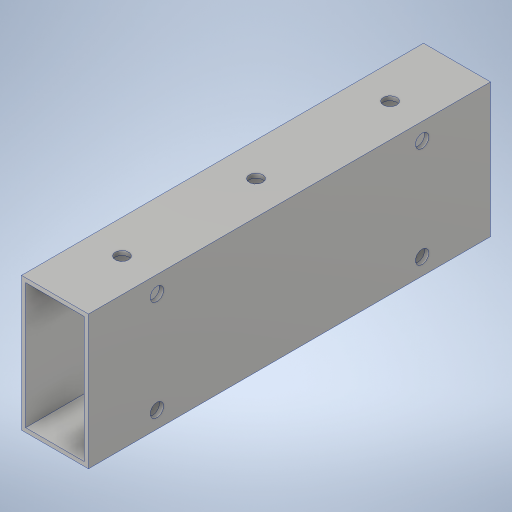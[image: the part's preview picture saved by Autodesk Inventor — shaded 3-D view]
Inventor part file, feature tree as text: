
AUTODESK INVENTOR PART (.ipt)
format: ipt  version: 2023.4 (Build 274418000, 418)  size: 261,632 bytes
history: native  units: in
note: dims shown in document units (in); Inventor stores cm internally (conversion verified against a paired STEP export)
features: hole x3, sketch x3, extrude x1, projected_geometry x1
ambient origin geometry x8: Origin, YZ Plane, XZ Plane, XY Plane, X Axis, Y Axis, Z Axis, Center Point
bodies: Solid1 (feature_tree)
feature tree (8):
  extrude  "Extrusion1"  Depth=4.0in
  hole  "Hole1"  [1 undecoded]
  hole  "Hole3"  [1 undecoded]
  hole  "Hole2"  [1 undecoded]
  sketch  "Sketch2"  dims[d4=0.0in d5=4.0in]
  projected_geometry  "Projected Loop1"
  sketch  "Sketch3"  dims[d6=0.201in d7=0.75in d8=0.385in d9=0.25in d10=0.5635in d11=1.0in d12=0.8108in d14=4.7244in]
  sketch  "Sketch4"  dims[d15=3.7402in d16=4.2323in d17=1.5in d18=0.156in d19=0.38in d20=0.375in d21=0.25in d22=0.5635in d23=1.0in d24=0.8108in d25=4.2323in d28=1.5in d29=0.201in d30=0.38in d31=0.385in d32=0.25in d33=0.5635in d34=1.0in d35=0.8108in]
note: 3 required parameter values undecoded (feature->parameter linkage not recoverable at this tier; creation-order binding heuristic only, values carry confidence <= 0.55)
